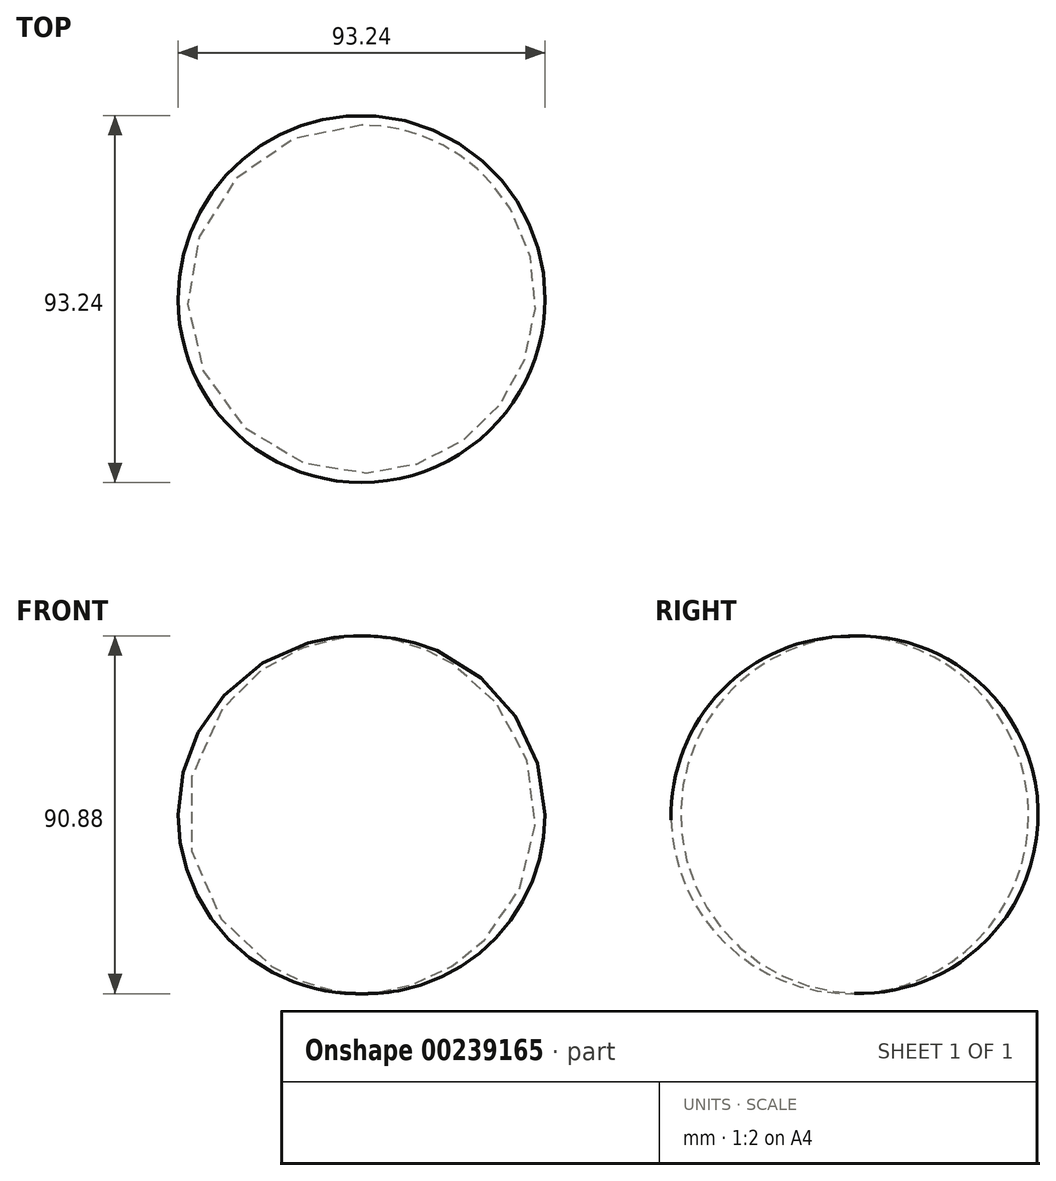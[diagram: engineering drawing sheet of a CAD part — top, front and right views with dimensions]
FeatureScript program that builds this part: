
annotation { "Feature Type Name" : "Feature", "Feature Type Description" : "" }
export const myFeature = defineFeature(function(context is Context, id is Id, definition is map)
    precondition{}
    {
        {
            var Q0;
            Q0=qCreatedBy(makeId("Right.planeOp"),FACE);
            var sketch = newSketch(context, id + "F0", { "sketchPlane" : qUnion([Q0])});
            skArc(sketch, "E0", {"start": v(2.43, -9.45) * mm, "mid": v(47.82, 37.17) * mm, "end": v(0, 81.3) * mm});
            skLineSegment(sketch, "E1", {"start": v(0, 81.3) * mm, "end": v(2.43, -9.45) * mm});
            skSolve(sketch);
        }
        {
            var Q0;
            Q0 = qSketchRegion(id + "F0", true);
            var Q1;
            Q1=sQuery(id+"F0.wireOp",EDGE,"E1");
            revolve(context, id + "F1", {"entities" : qUnion([Q0]), "axis" : qUnion([Q1]), "revolveType" : RevolveType.FULL});
        }
    });
